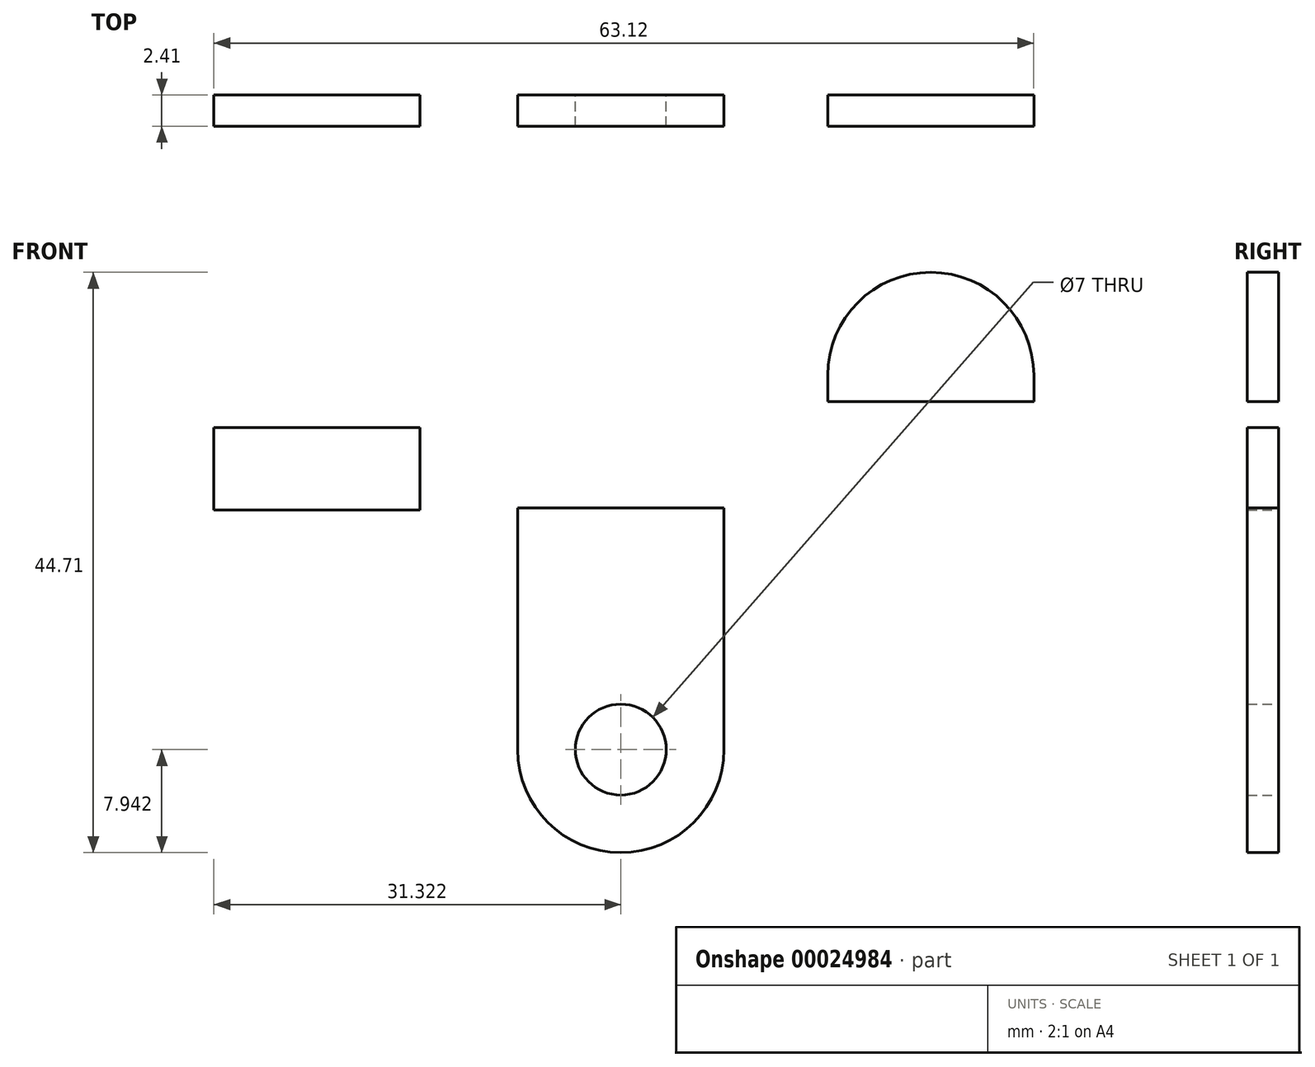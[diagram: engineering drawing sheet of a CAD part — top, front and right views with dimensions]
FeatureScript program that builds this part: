
annotation { "Feature Type Name" : "Feature", "Feature Type Description" : "" }
export const myFeature = defineFeature(function(context is Context, id is Id, definition is map)
    precondition{}
    {
        {
            var Q0;
            Q0=qCreatedBy(makeId("Front.planeOp"),FACE);
            var sketch = newSketch(context, id + "F0", { "sketchPlane" : qUnion([Q0])});
            skLineSegment(sketch, "E0.top", {"start": v(-7.94, -21.9) * mm, "end": v(-7.94, -21.9) * mm});
            skPoint(sketch, "E1.visualSharp", {"position": v(-15.87, -21.9) * mm});
            skArc(sketch, "E1.filletArc", {"start": v(-15.87, -13.96) * mm, "mid": v(-13.55, -19.57) * mm, "end": v(-7.94, -21.9) * mm});
            skPoint(sketch, "E2.visualSharp", {"position": v(0, -21.9) * mm});
            skArc(sketch, "E2.filletArc", {"start": v(-7.94, -21.9) * mm, "mid": v(-2.32, -19.57) * mm, "end": v(0, -13.96) * mm});
            skCircle(sketch, "E3", {"center": v(-7.94, -13.96) * mm, "radius": 3.5 * mm});
            skLineSegment(sketch, "E4.bottom", {"start": v(-15.87, -13.96) * mm, "end": v(0, -13.96) * mm});
            skLineSegment(sketch, "E4.top", {"start": v(-15.88, 4.66) * mm, "end": v(0, 4.66) * mm});
            skLineSegment(sketch, "E4.left", {"start": v(-15.87, -13.96) * mm, "end": v(-15.87, 4.66) * mm});
            skLineSegment(sketch, "E4.right", {"start": v(0, -13.96) * mm, "end": v(0, 4.66) * mm});
            skLineSegment(sketch, "E5.bottom", {"start": v(-39.26, 10.84) * mm, "end": v(-23.38, 10.84) * mm});
            skLineSegment(sketch, "E5.top", {"start": v(-39.26, 4.51) * mm, "end": v(-23.38, 4.51) * mm});
            skLineSegment(sketch, "E5.left", {"start": v(-39.26, 10.84) * mm, "end": v(-39.26, 4.51) * mm});
            skLineSegment(sketch, "E5.right", {"start": v(-23.38, 10.84) * mm, "end": v(-23.38, 4.51) * mm});
            skLineSegment(sketch, "E6.bottom", {"start": v(7.99, 12.85) * mm, "end": v(23.86, 12.85) * mm});
            skLineSegment(sketch, "E6.top", {"start": v(15.93, 22.8) * mm, "end": v(15.93, 22.8) * mm});
            skLineSegment(sketch, "E6.left", {"start": v(7.99, 12.85) * mm, "end": v(7.99, 14.87) * mm});
            skLineSegment(sketch, "E6.right", {"start": v(23.86, 12.85) * mm, "end": v(23.86, 14.87) * mm});
            skPoint(sketch, "E7.visualSharp", {"position": v(7.99, 22.8) * mm});
            skArc(sketch, "E7.filletArc", {"start": v(15.93, 22.8) * mm, "mid": v(10.31, 20.48) * mm, "end": v(7.99, 14.87) * mm});
            skPoint(sketch, "E8.visualSharp", {"position": v(23.86, 22.8) * mm});
            skArc(sketch, "E8.filletArc", {"start": v(23.86, 14.87) * mm, "mid": v(21.54, 20.48) * mm, "end": v(15.93, 22.8) * mm});
            skSolve(sketch);
        }
        {
            var Q0;
            Q0 = qSketchRegion(id + "F0", true);
            extrude(context, id + "F1", {"entities" : qUnion([Q0]), "depth" : 2.41 * mm});
        }
    });
